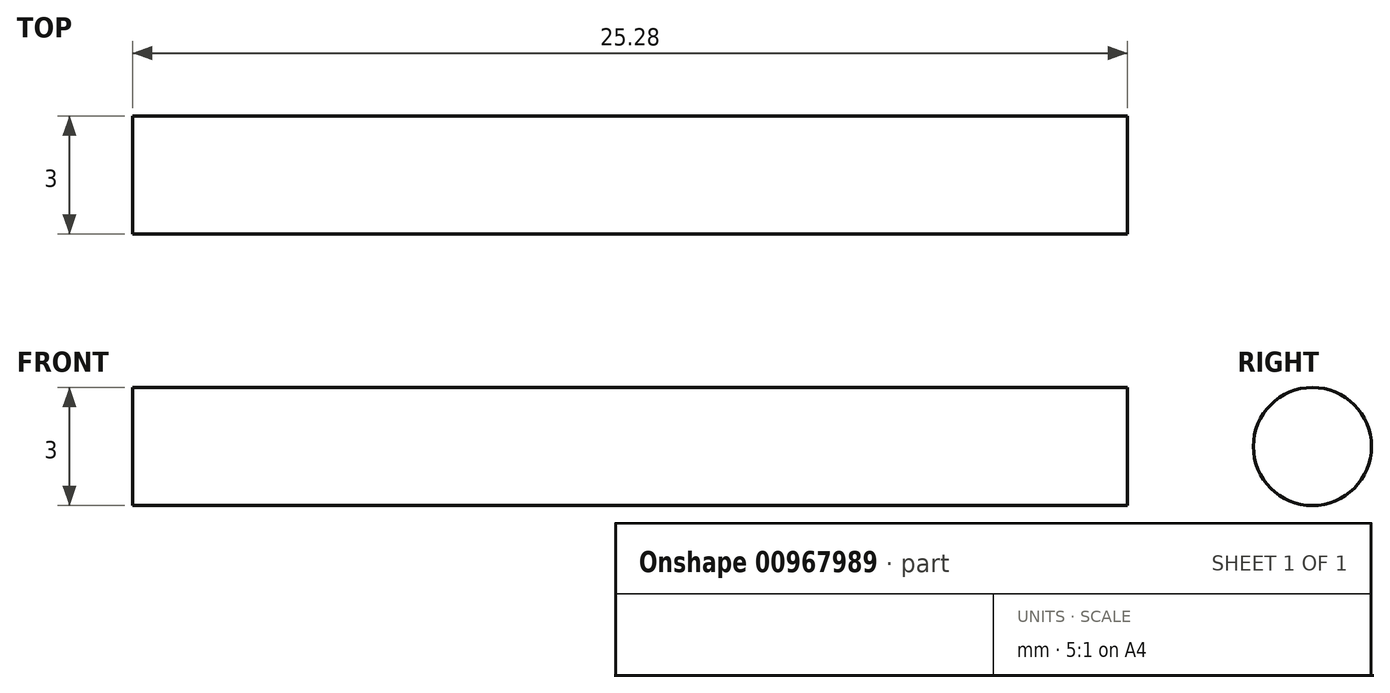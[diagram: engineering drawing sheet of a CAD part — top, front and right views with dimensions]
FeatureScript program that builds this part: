
annotation { "Feature Type Name" : "Feature", "Feature Type Description" : "" }
export const myFeature = defineFeature(function(context is Context, id is Id, definition is map)
    precondition{}
    {
        {
            var Q0;
            Q0=qCreatedBy(makeId("Front.planeOp"),FACE);
            var sketch = newSketch(context, id + "F0", { "sketchPlane" : qUnion([Q0])});
            skLineSegment(sketch, "E0.bottom", {"start": v(12.64, -0.75) * mm, "end": v(-12.64, -0.75) * mm});
            skLineSegment(sketch, "E0.top", {"start": v(12.64, 0.75) * mm, "end": v(-12.64, 0.75) * mm});
            skLineSegment(sketch, "E0.left", {"start": v(12.64, -0.75) * mm, "end": v(12.64, 0.75) * mm});
            skLineSegment(sketch, "E0.right", {"start": v(-12.64, -0.75) * mm, "end": v(-12.64, 0.75) * mm});
            skPoint(sketch, "E0.middle", {"position": v(0, 0) * mm});
            skSolve(sketch);
        }
        {
            var Q0;
            Q0=makeQuery(id+"F0.imprint","IMPRINT",FACE,{"disambiguationData":[TD([[makeQuery(id+"F0.imprint","IMPRINT",EDGE,{"derivedFrom":sQuery(id+"F0.wireOp",EDGE,"E0.bottom")}),-1.0]])]});
            var Q1;
            Q1=sQuery(id+"F0.wireOp",EDGE,"E0.bottom");
            revolve(context, id + "F1", {"surfaceOperationType" : NewSurfaceOperationType.NEW, "entities" : qUnion([Q0]), "axis" : qUnion([Q1]), "revolveType" : RevolveType.FULL});
        }
    });
